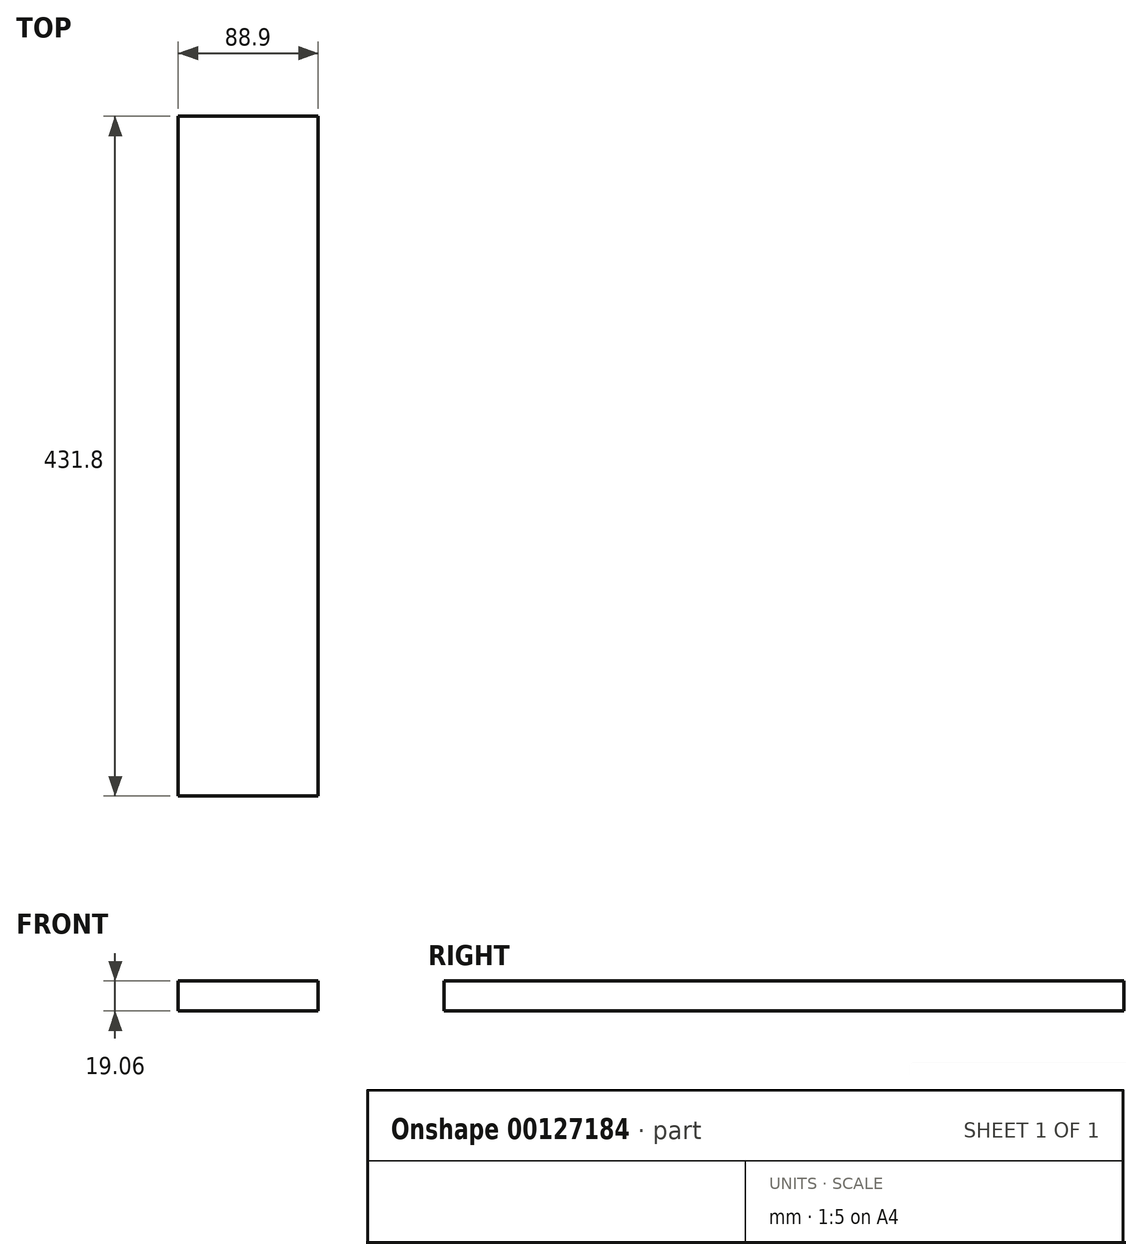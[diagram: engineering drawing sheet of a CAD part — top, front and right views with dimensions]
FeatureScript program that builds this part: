
annotation { "Feature Type Name" : "Feature", "Feature Type Description" : "" }
export const myFeature = defineFeature(function(context is Context, id is Id, definition is map)
    precondition{}
    {
        {
            var Q0;
            Q0=qCreatedBy(makeId("Front.planeOp"),FACE);
            var sketch = newSketch(context, id + "F0", { "sketchPlane" : qUnion([Q0])});
            skLineSegment(sketch, "E0.bottom", {"start": v(44.45, -9.52) * mm, "end": v(-44.45, -9.53) * mm});
            skLineSegment(sketch, "E0.top", {"start": v(44.45, 9.53) * mm, "end": v(-44.45, 9.53) * mm});
            skLineSegment(sketch, "E0.left", {"start": v(44.45, -9.52) * mm, "end": v(44.45, 9.53) * mm});
            skLineSegment(sketch, "E0.right", {"start": v(-44.45, -9.53) * mm, "end": v(-44.45, 9.53) * mm});
            skPoint(sketch, "E0.middle", {"position": v(0, 0) * mm});
            skSolve(sketch);
        }
        {
            var Q0;
            Q0=qSketchRegion(id+"F0",true);
            extrude(context, id + "F1", {"entities" : qUnion([Q0]), "depth" : 431.8 * mm});
        }
    });
